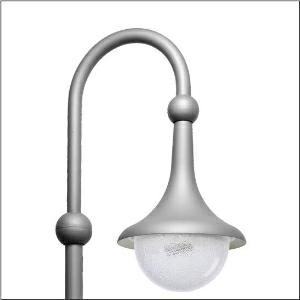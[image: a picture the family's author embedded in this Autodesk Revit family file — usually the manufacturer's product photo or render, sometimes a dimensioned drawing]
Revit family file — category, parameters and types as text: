
# Revit family: grosse_glocke___st1_2a_5xa1563k1b208_bcd9
name_source: partatom
category: Lighting Fixtures
units: mm (PartAtom-declared; Revit-internal decimal feet)

## family parameters
Cut with Voids When Loaded = No
Host = Face
Light Source = No
Part Type = Normal
Room Calculation Point = No
Round Connector Dimension = Use Diameter
Shared = No

## types (1)
- --- (1 x LED, 3380 lm, 23.4 W, 4000K)
    Apparent Load = 23 VA
    CIE Flux Codes = 29 66 94 99 100
    Color Rendering = 70
    Color Temperature = 4000K
    Default Elevation = 1800 mm
    Description = Large Bell, mast luminaire, primary light control with 3 zone facetted reflector, of plastic, silver coated, primary optical cover: enclosure, of PMMA, transparent structured, light distribution: ST1.2a, light emission: direct distribution, primary light characteristic: asymmetric, installation type: suspended mounting, LED, High Power LED, rated luminous flux: 3.380lm, luminous efficacy: 144lm/W, light colour: 740, colour temperature: 4000K, control gear: ECG Plus, control: flexible luminous flux parameterisation, time-dependent luminous flux control, constant luminous flux control, digital communication interface, power reduction, electronic power reduction, mains connection: 230..240V, AC, 50/60Hz, start of lifetime: 23W, end of service life: 24W, reduction: 12W, luminaire housing, bell-shaped, of glass-fibre reinforced polyester, coated, Siteco® metallic grey (DB 702S), please order curved mast extension separately, diameter: 530mm, height: 695mm, protection rating (complete): IP54, insulation class (complete): insulation class II (safety insulation), certification: CE, ENEC, VDE, impact resistance: IK08, standard-compliant lighting for roads and squares, packaging unit: 1 piece

Light Distribution: ST1.2a
    Height = 695 mm
    Lamp = 1 x LED
    Lamp Light Flux = 3380 lm
    Lamp Power = 23.4 W
    Lamp count = 1
    Length = 530 mm
    Luminous efficacy = 144 lm/W
    Manufacturer = Siteco
    ModVariant = No
    Model = 5XA1563K1B208
    Number of Poles = 1
    OnlyDefault = Yes
    Power Factor = 1
    Product Name = Große Glocke | ST1.2a
    Product group = mast luminaire | pylon annexe
    ProductGroupID = 6201
    Protection Class = Protection class II
    Protection Degree = IP 54
    RLX_Detail_Level = 1
    RLX_Emergency_Light_Flux = 0 lm
    RLX_Emergency_Type = 0
    RLX_Emergency_Type_DB = No
    RlxData = <blob elided: 54649 chars, md5=76e77131>
    Socket = socket
    Standby Power = 0 W
    System Light Flux = 3380 lm
    System Power = 23 W
    Type Comments = factory setting: luminous flux: 100 % | dim-lin: 254 | 460 mA
    Type Image = l_1284387.jpg
    URL = http://relux.com
    VarID = @adj_137403
    Voltage = 0 V
    Weight = 0.00 kg
    Width = 0 mm  [stored 0 ft]

note: [stored X ft] marks values corroborated as IEEE doubles in the binary element streams (Revit-internal decimal feet)

## geometry (parser evidence)
native form markers: Blend x4, Sweep x10
no freeform markers — native parametric forms only
